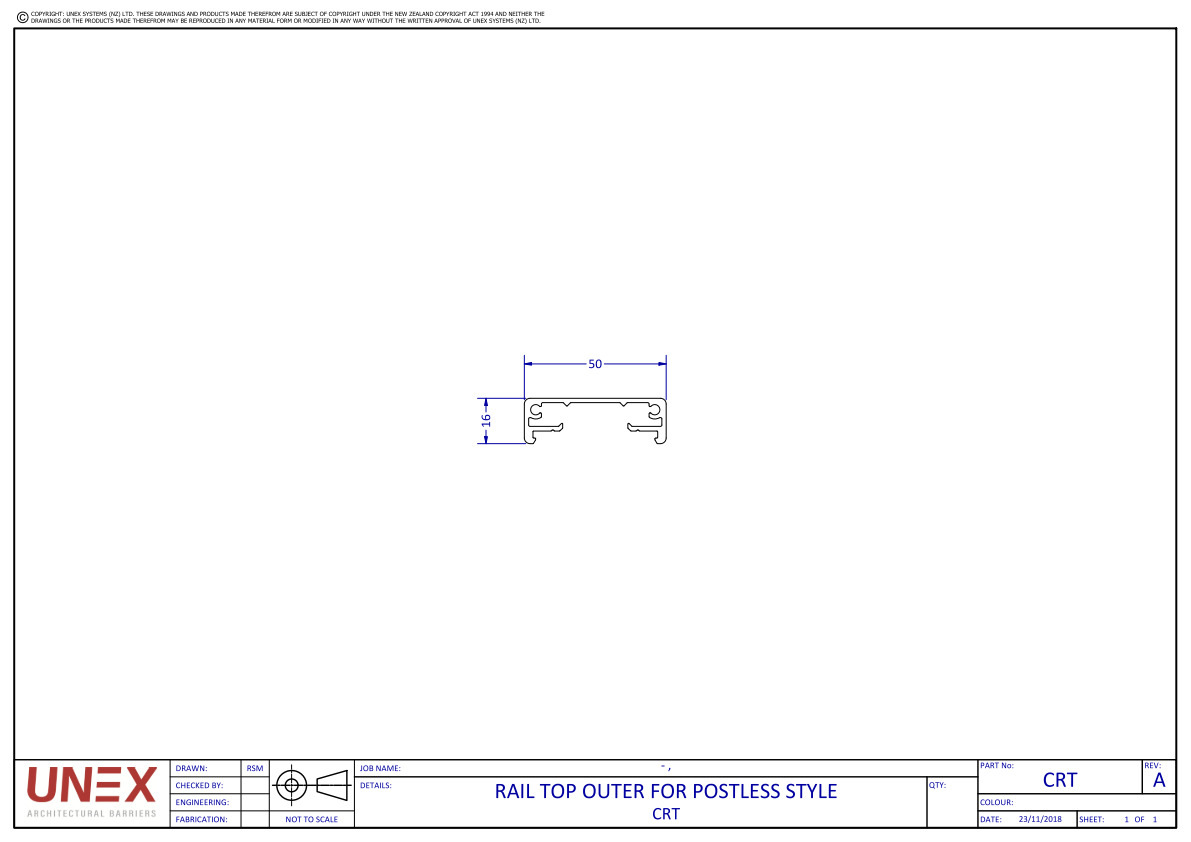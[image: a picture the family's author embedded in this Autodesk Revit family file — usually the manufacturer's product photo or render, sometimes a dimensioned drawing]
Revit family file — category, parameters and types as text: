
# Revit family: POSTLESS
name_source: partatom
category: Generic Models
units: mm (PartAtom-declared; Revit-internal decimal feet)

## family parameters
Always vertical = Yes
Can host rebar = No
Cut with Voids When Loaded = No
Part Type = Normal
Room Calculation Point = No
Round Connector Dimension = Use Diameter
Shared = No
Work Plane-Based = No

## types (1)
- POSTLESS
    Above fin height = 1784 mm
    Actual Fin QTY = 25
    Below Fin Height = 250 mm  [stored 0.82021 ft]
    Default Elevation = 0 mm  [stored 0 ft]
    Description = UENEX SYSTEMS  POSTLESS FINLINE SIDE FIXED
    Ground Height = 1800 mm  [stored 5.90551 ft]
    Keynote = UENEX SYSTEMS  POSTLESS FINLINE
    Length = 2500 mm  [stored 8.2021 ft]
    Manufacturer = UNEX SYTEMS
    Max Fin Space = 25
    Model = POSTLESS FINELINE
    Top Rail Off Set = 50 mm  [stored 0.164042 ft]
    Total Height = 2214 mm
    URL = WWW.UNEX.CO.NZ

note: [stored X ft] marks values corroborated as IEEE doubles in the binary element streams (Revit-internal decimal feet)

## geometry (parser evidence)
native form markers: Sweep x11
no freeform markers — native parametric forms only
